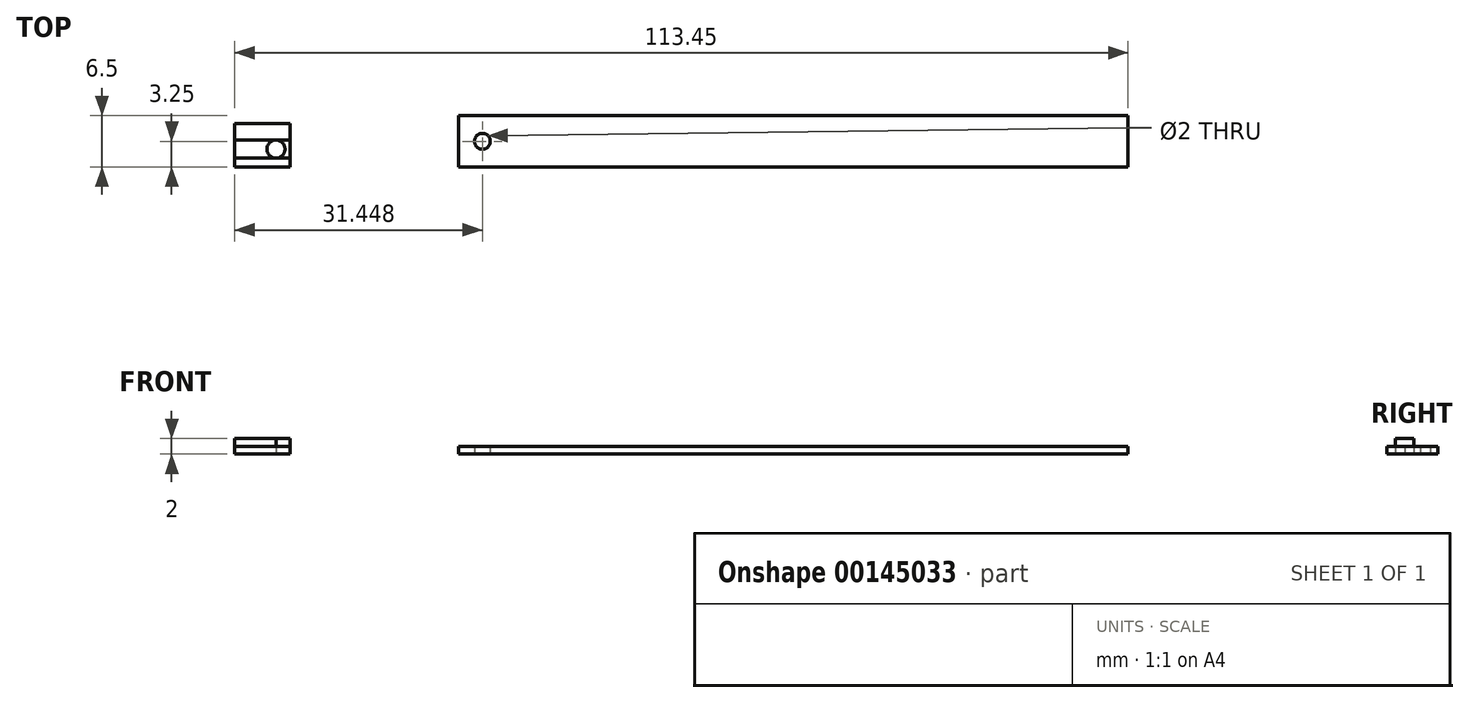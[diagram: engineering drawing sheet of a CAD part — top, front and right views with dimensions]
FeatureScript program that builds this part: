
annotation { "Feature Type Name" : "Feature", "Feature Type Description" : "" }
export const myFeature = defineFeature(function(context is Context, id is Id, definition is map)
    precondition{}
    {
        {
            var Q0;
            Q0=qCreatedBy(makeId("Top.planeOp"),FACE);
            var sketch = newSketch(context, id + "F0", { "sketchPlane" : qUnion([Q0])});
            skLineSegment(sketch, "E0.bottom", {"start": v(89.44, 0) * mm, "end": v(4.44, 0) * mm});
            skLineSegment(sketch, "E0.top", {"start": v(89.44, 6.5) * mm, "end": v(4.44, 6.5) * mm});
            skLineSegment(sketch, "E0.left", {"start": v(89.44, 0) * mm, "end": v(89.44, 6.5) * mm});
            skLineSegment(sketch, "E0.right", {"start": v(4.44, 0) * mm, "end": v(4.44, 6.5) * mm});
            skLineSegment(sketch, "E1", {"start": v(7.44, 10.07) * mm, "end": v(7.44, -6.68) * mm, "construction": true});
            skLineSegment(sketch, "E2", {"start": v(2.48, 3.25) * mm, "end": v(14.02, 3.25) * mm, "construction": true});
            skPoint(sketch, "E2.startSnap0", {"position": v(4.44, 3.25) * mm});
            skPoint(sketch, "E3", {"position": v(7.44, 3.25) * mm});
            skCircle(sketch, "E4", {"center": v(7.44, 3.25) * mm, "radius": 1 * mm});
            skSolve(sketch);
        }
        {
            var Q0;
            Q0=makeQuery(id+"F0.imprint","IMPRINT",FACE,{"disambiguationData":[TD([[makeQuery(id+"F0.imprint","IMPRINT",EDGE,{"derivedFrom":sQuery(id+"F0.wireOp",EDGE,"E0.bottom")}),-1.0]])]});
            extrude(context, id + "F1", {"entities" : qUnion([Q0]), "depth" : 1 * mm});
        }
        {
            var Q0;
            Q0=qCreatedBy(makeId("Top.planeOp"),FACE);
            var sketch = newSketch(context, id + "F2", { "sketchPlane" : qUnion([Q0])});
            skLineSegment(sketch, "E5.bottom", {"start": v(-17, 0) * mm, "end": v(-24, 0) * mm});
            skLineSegment(sketch, "E5.top", {"start": v(-17, 5.5) * mm, "end": v(-24, 5.5) * mm});
            skLineSegment(sketch, "E5.left", {"start": v(-17, 0) * mm, "end": v(-17, 5.5) * mm});
            skLineSegment(sketch, "E5.right", {"start": v(-24, 0) * mm, "end": v(-24, 5.5) * mm});
            skLineSegment(sketch, "E6", {"start": v(-24, 3.4) * mm, "end": v(-17, 3.4) * mm});
            skLineSegment(sketch, "E7", {"start": v(-24, 1.1) * mm, "end": v(-17, 1.1) * mm});
            skCircle(sketch, "E8", {"center": v(-18.78, 2.25) * mm, "radius": 1.15 * mm});
            skPoint(sketch, "E8.first.point", {"position": v(-18.78, 3.4) * mm});
            skPoint(sketch, "E8.second.point", {"position": v(-18.78, 1.1) * mm});
            skPoint(sketch, "E8.third.point", {"position": v(-17.64, 2.34) * mm});
            skSolve(sketch);
        }
        {
            var Q0;
            {var subQ1=sQuery(id+"F2.wireOp",EDGE,"E5.top");Q0=makeQuery(id+"F2.imprint","IMPRINT",FACE,{"disambiguationData":[TD([[makeQuery(id+"F2.imprint","IMPRINT",EDGE,{"derivedFrom":subQ1}),1.0]])]});}
            var Q1;
            {var subQ1=sQuery(id+"F2.wireOp",EDGE,"E5.bottom");Q1=makeQuery(id+"F2.imprint","IMPRINT",FACE,{"disambiguationData":[TD([[makeQuery(id+"F2.imprint","IMPRINT",EDGE,{"derivedFrom":subQ1}),-1.0]])]});}
            extrude(context, id + "F3", {"entities" : qUnion([Q0, Q1]), "depth" : 1 * mm});
        }
        {
            var Q0;
            {var subQ0=sQuery(id+"F2.wireOp",EDGE,"E6");var subQ1=sQuery(id+"F2.wireOp",EDGE,"E5.right");var subQ2=makeQuery(id+"F2.imprint","INTERSECT",VERTEX,{"derivedFrom":[subQ1,subQ0]});Q0=makeQuery(id+"F2.imprint","IMPRINT",FACE,{"disambiguationData":[TD([[makeQuery(id+"F2.imprint","IMPRINT",EDGE,{"disambiguationData":[TD([[subQ2,1.0]])],"derivedFrom":subQ1}),-1.0]])]});}
            var Q1;
            {var subQ0=sQuery(id+"F2.wireOp",EDGE,"E6");var subQ1=sQuery(id+"F2.wireOp",EDGE,"E5.left");var subQ2=makeQuery(id+"F2.imprint","INTERSECT",VERTEX,{"derivedFrom":[subQ1,subQ0]});Q1=makeQuery(id+"F2.imprint","IMPRINT",FACE,{"disambiguationData":[TD([[makeQuery(id+"F2.imprint","IMPRINT",EDGE,{"disambiguationData":[TD([[subQ2,1.0]])],"derivedFrom":subQ1}),1.0]])]});}
            extrude(context, id + "F4", {"entities" : qUnion([Q0, Q1]), "depth" : 2 * mm});
        }
    });
